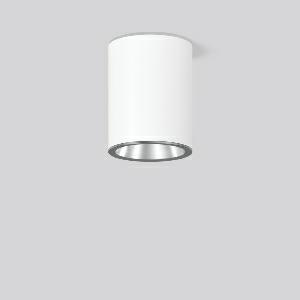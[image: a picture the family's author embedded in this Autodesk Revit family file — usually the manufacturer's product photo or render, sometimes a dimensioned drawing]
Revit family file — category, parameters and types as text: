
# Revit family: andho_mini_931251_002_2_76_7837
name_source: partatom
category: Lighting Fixtures
units: mm (PartAtom-declared; Revit-internal decimal feet)

## family parameters
Cut with Voids When Loaded = No
Host = Face
Light Source = No
Part Type = Normal
Room Calculation Point = No
Round Connector Dimension = Use Diameter
Shared = No

## types (1)
- ANDHO mini (1 x LED Modul 827, 2800 lm, 2700)
    Apparent Load = 27 VA
    CIE Flux Codes = 96 100 100 100 100
    Color Rendering = 80
    Color Temperature = 2700
    Default Elevation = 1800 mm
    Description = Series: ANDHO mini
High-quality surface-mounted downlight for indoor and outdoor use. Housing made of corrosion-resistant die-cast aluminium, seawater resistant powder-coated. With membrane valve as a standard to avoid condensed water. Cover clear single-pane toughened glass. Rotation-symmetric reflector made of reflex-boosted MIRO-SILVER. Easy installation with a separate ceiling frame and plug connection. 5 pole double terminal for through-wiring. 
Colour: traffic white, matt (RAL 9016)
Diameter: 114 mm
Height: 147 mm
Lamp: LED
Socket: without socket
Colour temperature: 2700K
Colour rendering index (CRI): 80
System power: 27 W
Rated luminous flux: 2800 lm
Beam angle Down: 40°
Luminous efficiency: 104 lm/W
Control gear: Converter, dimmable, DALI
Protection class: I
Type of protection: IP 66
    Height = 147 mm
    Lamp = 1 x LED Modul 827
    Lamp Light Flux = 2800 lm
    Lamp count = 1
    Length = 114 mm
    Lifetime = 50000 h
    Luminous efficacy = 104 lm/W
    Manufacturer = RZB
    ModVariant = No
    Model = 931251.002.2.76
    Mounting Place = Ceiling
    Mounting Type = Surface mounted
    Number of Poles = 1
    OnlyDefault = Yes
    Power Factor = 1
    Product Name = ANDHO mini
    Product group = Surface mounted downlights
    ProductGroupID = 302
    Protection Class = Protection class I
    Protection Degree = Degree of protection
    RLX_Detail_Level = 1
    RLX_Emergency_Light_Flux = 0 lm
    RLX_Emergency_Type = 0
    RLX_Emergency_Type_DB = No
    RlxData = <blob elided: 22449 chars, md5=d2ec4a61>
    Socket = socket
    Standby Power = 0 W
    System Light Flux = 2800 lm
    System Power = 27 W
    Type Comments = ALEA SPOT
    Type Image = 931251.002.jpg
    URL = http://relux.com
    VarID = ---
    Voltage = 0 V
    Weight = 0.00 kg
    Width = 0 mm  [stored 0 ft]

note: [stored X ft] marks values corroborated as IEEE doubles in the binary element streams (Revit-internal decimal feet)

## geometry (parser evidence)
native form markers: Blend x4, Sweep x11
no freeform markers — native parametric forms only
